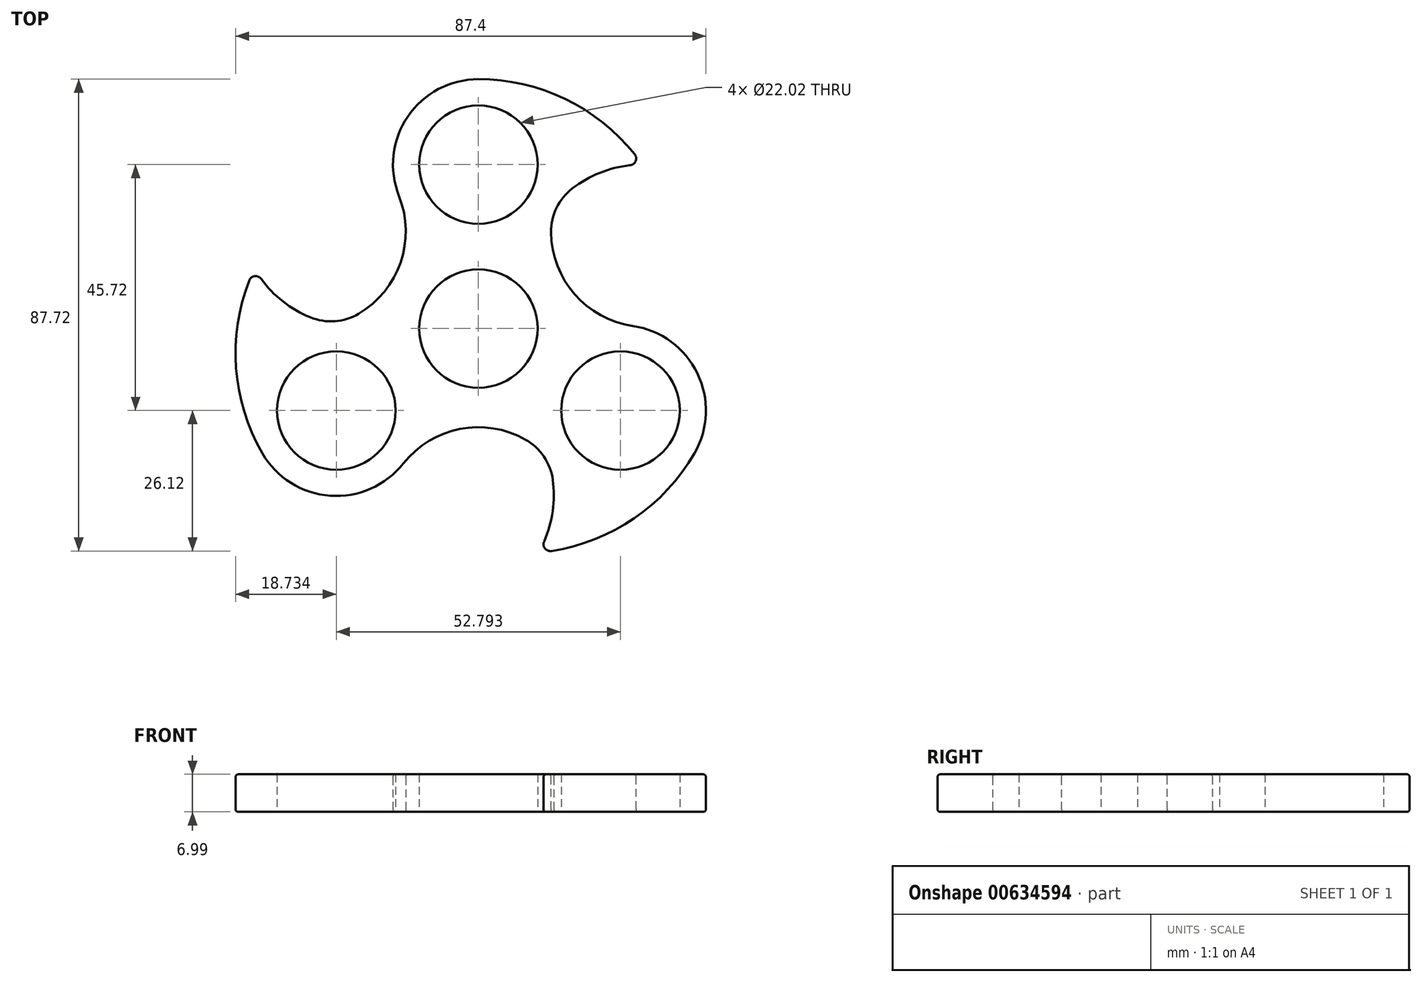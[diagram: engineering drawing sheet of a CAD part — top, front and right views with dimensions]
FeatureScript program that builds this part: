
annotation { "Feature Type Name" : "Feature", "Feature Type Description" : "" }
export const myFeature = defineFeature(function(context is Context, id is Id, definition is map)
    precondition{}
    {
        {
            var Q0;
            Q0=qCreatedBy(makeId("Top.planeOp"),FACE);
            var sketch = newSketch(context, id + "F0", { "sketchPlane" : qUnion([Q0])});
            skCircle(sketch, "E0", {"center": v(0, 0) * mm, "radius": 11.01 * mm});
            skLineSegment(sketch, "E1", {"start": v(0, 0) * mm, "end": v(0, 30.48) * mm});
            skLineSegment(sketch, "E2", {"start": v(0, 0) * mm, "end": v(26.4, -15.24) * mm});
            skLineSegment(sketch, "E3", {"start": v(0, 0) * mm, "end": v(-26.4, -15.24) * mm});
            skCircle(sketch, "E4", {"center": v(0, 30.48) * mm, "radius": 11.01 * mm});
            skCircle(sketch, "E5", {"center": v(26.4, -15.24) * mm, "radius": 11.01 * mm});
            skCircle(sketch, "E6", {"center": v(-26.4, -15.24) * mm, "radius": 11.01 * mm});
            skCircle(sketch, "E7", {"center": v(0, 30.48) * mm, "radius": 15.88 * mm});
            skArc(sketch, "E8", {"start": v(30.48, 30.48) * mm, "mid": v(17.18, 42.15) * mm, "end": v(0, 46.35) * mm});
            skArc(sketch, "E9", {"start": v(30.48, 30.48) * mm, "mid": v(20.63, 28.07) * mm, "end": v(13, 21.38) * mm});
            skLineSegment(sketch, "E10", {"start": v(0, 30.48) * mm, "end": v(30.48, 30.48) * mm});
            skCircle(sketch, "E11.1.1", {"center": v(-26.4, -15.24) * mm, "radius": 15.88 * mm});
            skLineSegment(sketch, "E11.1.2", {"start": v(-26.4, -15.24) * mm, "end": v(-41.64, 11.16) * mm});
            skArc(sketch, "E11.1.3", {"start": v(-41.64, 11.16) * mm, "mid": v(-45.1, -6.2) * mm, "end": v(-40.14, -23.18) * mm});
            skArc(sketch, "E11.1.4", {"start": v(-41.64, 11.16) * mm, "mid": v(-34.62, 3.83) * mm, "end": v(-25.02, 0.58) * mm});
            skCircle(sketch, "E11.2.1", {"center": v(26.4, -15.24) * mm, "radius": 15.88 * mm});
            skLineSegment(sketch, "E11.2.2", {"start": v(26.4, -15.24) * mm, "end": v(11.16, -41.64) * mm});
            skArc(sketch, "E11.2.3", {"start": v(11.16, -41.64) * mm, "mid": v(27.9, -35.96) * mm, "end": v(40.14, -23.18) * mm});
            skArc(sketch, "E11.2.4", {"start": v(11.16, -41.64) * mm, "mid": v(14, -31.9) * mm, "end": v(12.01, -21.96) * mm});
            skArc(sketch, "E12", {"start": v(-28.7, 0.47) * mm, "mid": v(-15.88, 9.17) * mm, "end": v(-14.75, 24.62) * mm});
            skArc(sketch, "E13", {"start": v(14.75, 24.62) * mm, "mid": v(15.88, 9.17) * mm, "end": v(28.7, 0.47) * mm});
            skArc(sketch, "E14", {"start": v(13.95, -25.09) * mm, "mid": v(0, -18.34) * mm, "end": v(-13.95, -25.09) * mm});
            skSolve(sketch);
        }
        {
            var Q0;
            Q0 = qSketchRegion(id + "F0", true);
            var Q1;
            {var subQ0=sQuery(id+"F0.wireOp",EDGE,"E11.1.1");var subQ2=sQuery(id+"F0.wireOp",EDGE,"E3");var subQ3=makeQuery(id+"F0.imprint","INTERSECT",VERTEX,{"derivedFrom":[subQ2,subQ0]});Q1=makeQuery(id+"F0.imprint","IMPRINT",FACE,{"disambiguationData":[TD([[makeQuery(id+"F0.imprint","IMPRINT",EDGE,{"disambiguationData":[TD([[subQ3,-1.0]])],"derivedFrom":subQ2}),-1.0]])]});}
            var Q2;
            {var subQ0=sQuery(id+"F0.wireOp",EDGE,"E7");var subQ4=sQuery(id+"F0.wireOp",EDGE,"E1");var subQ8=makeQuery(id+"F0.imprint","INTERSECT",VERTEX,{"derivedFrom":[subQ4,subQ0]});Q2=makeQuery(id+"F0.imprint","IMPRINT",FACE,{"disambiguationData":[TD([[makeQuery(id+"F0.imprint","IMPRINT",EDGE,{"disambiguationData":[TD([[subQ8,-1.0]])],"derivedFrom":subQ4}),-1.0]])]});}
            var Q3;
            {var subQ0=sQuery(id+"F0.wireOp",EDGE,"E11.2.1");var subQ2=sQuery(id+"F0.wireOp",EDGE,"E2");var subQ3=makeQuery(id+"F0.imprint","INTERSECT",VERTEX,{"derivedFrom":[subQ2,subQ0]});Q3=makeQuery(id+"F0.imprint","IMPRINT",FACE,{"disambiguationData":[TD([[makeQuery(id+"F0.imprint","IMPRINT",EDGE,{"disambiguationData":[TD([[subQ3,-1.0]])],"derivedFrom":subQ2}),-1.0]])]});}
            extrude(context, id + "F1", {"entities" : qUnion([Q0, Q1, Q2, Q3]), "depth" : 7 * mm, "offsetDistance" : 25.4 * mm});
        }
        {
            var Q0;
            Q0=makeQuery(id+"F1.opExtrude","SWEPT_EDGE",EDGE,{"disambiguationData":[OSD([sQuery(id+"F0.wireOp",EDGE,"E11.2.4"),sQuery(id+"F0.wireOp",EDGE,"E14")])]});
            var Q1;
            Q1=makeQuery(id+"F1.opExtrude","SWEPT_EDGE",EDGE,{"disambiguationData":[OSD([sQuery(id+"F0.wireOp",EDGE,"E11.1.4"),sQuery(id+"F0.wireOp",EDGE,"E12")])]});
            var Q2;
            Q2=makeQuery(id+"F1.opExtrude","SWEPT_EDGE",EDGE,{"disambiguationData":[OSD([sQuery(id+"F0.wireOp",EDGE,"E9"),sQuery(id+"F0.wireOp",EDGE,"E13")])]});
            fillet(context, id + "F2", {"entities" : qUnion([Q0, Q1, Q2]), "radius" : 10.16 * mm, "tangentPropagation" : true, "allowEdgeOverflow" : false});
        }
        {
            var Q0;
            Q0=makeQuery(id+"F1.opExtrude","SWEPT_EDGE",EDGE,{"disambiguationData":[OSD([sQuery(id+"F0.wireOp",EDGE,"E11.1.2"),sQuery(id+"F0.wireOp",EDGE,"E11.1.3"),sQuery(id+"F0.wireOp",EDGE,"E11.1.4")])]});
            var Q1;
            Q1=makeQuery(id+"F1.opExtrude","SWEPT_EDGE",EDGE,{"disambiguationData":[OSD([sQuery(id+"F0.wireOp",EDGE,"E11.2.2"),sQuery(id+"F0.wireOp",EDGE,"E11.2.3"),sQuery(id+"F0.wireOp",EDGE,"E11.2.4")])]});
            var Q2;
            Q2=makeQuery(id+"F1.opExtrude","SWEPT_EDGE",EDGE,{"disambiguationData":[OSD([sQuery(id+"F0.wireOp",EDGE,"E8"),sQuery(id+"F0.wireOp",EDGE,"E9"),sQuery(id+"F0.wireOp",EDGE,"E10")])]});
            fillet(context, id + "F3", {"entities" : qUnion([Q0, Q1, Q2]), "radius" : 1.27 * mm, "tangentPropagation" : true, "allowEdgeOverflow" : false});
        }
        {
            var Q0;
            Q0=makeQuery(id+"F1.opExtrude","CAP_EDGE",EDGE,{"disambiguationData":[OSD([sQuery(id+"F0.wireOp",EDGE,"E12")])],"isStart":false});
            fillet(context, id + "F4", {"entities" : qUnion([Q0]), "radius" : 0.5 * mm, "tangentPropagation" : true, "allowEdgeOverflow" : false});
        }
        {
            var Q0;
            Q0=makeQuery(id+"F1.opExtrude","CAP_EDGE",EDGE,{"disambiguationData":[OSD([sQuery(id+"F0.wireOp",EDGE,"E8")])],"isStart":true});
            fillet(context, id + "F5", {"entities" : qUnion([Q0]), "radius" : 0.5 * mm, "tangentPropagation" : true, "allowEdgeOverflow" : false});
        }
    });
